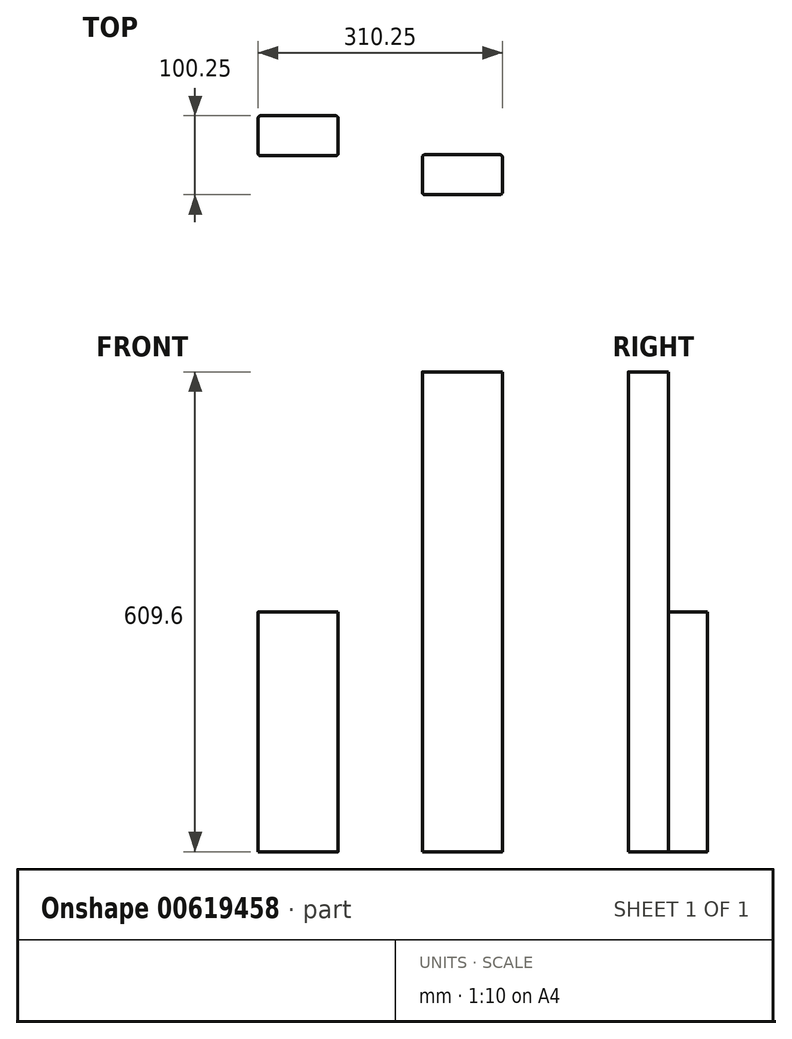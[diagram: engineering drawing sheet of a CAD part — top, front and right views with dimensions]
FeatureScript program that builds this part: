
annotation { "Feature Type Name" : "Feature", "Feature Type Description" : "" }
export const myFeature = defineFeature(function(context is Context, id is Id, definition is map)
    precondition{}
    {
        {
            var Q0;
            Q0=qCreatedBy(makeId("Top.planeOp"),FACE);
            var sketch = newSketch(context, id + "F0", { "sketchPlane" : qUnion([Q0])});
            skLineSegment(sketch, "E0.bottom", {"start": v(47.63, -25.4) * mm, "end": v(-47.63, -25.4) * mm});
            skLineSegment(sketch, "E0.top", {"start": v(47.63, 25.4) * mm, "end": v(-47.63, 25.4) * mm});
            skLineSegment(sketch, "E0.left", {"start": v(50.8, -22.22) * mm, "end": v(50.8, 22.23) * mm});
            skLineSegment(sketch, "E0.right", {"start": v(-50.8, -22.23) * mm, "end": v(-50.8, 22.22) * mm});
            skPoint(sketch, "E0.middle", {"position": v(0, 0) * mm});
            skPoint(sketch, "E1.visualSharp", {"position": v(-50.8, 25.4) * mm});
            skArc(sketch, "E1.filletArc", {"start": v(-47.63, 25.4) * mm, "mid": v(-49.87, 24.47) * mm, "end": v(-50.8, 22.22) * mm});
            skPoint(sketch, "E2.visualSharp", {"position": v(50.8, 25.4) * mm});
            skArc(sketch, "E2.filletArc", {"start": v(50.8, 22.23) * mm, "mid": v(49.87, 24.47) * mm, "end": v(47.63, 25.4) * mm});
            skPoint(sketch, "E3.visualSharp", {"position": v(50.8, -25.4) * mm});
            skArc(sketch, "E3.filletArc", {"start": v(47.63, -25.4) * mm, "mid": v(49.87, -24.47) * mm, "end": v(50.8, -22.22) * mm});
            skPoint(sketch, "E4.visualSharp", {"position": v(-50.8, -25.4) * mm});
            skArc(sketch, "E4.filletArc", {"start": v(-50.8, -22.23) * mm, "mid": v(-49.87, -24.47) * mm, "end": v(-47.63, -25.4) * mm});
            skSolve(sketch);
        }
        {
            var Q0;
            Q0 = qSketchRegion(id + "F0", true);
            extrude(context, id + "F1", {"entities" : qUnion([Q0]), "depth" : 304.8 * mm, "offsetDistance" : 25.4 * mm});
        }
        {
            var Q0;
            Q0=qCreatedBy(makeId("Top.planeOp"),FACE);
            var sketch = newSketch(context, id + "F2", { "sketchPlane" : qUnion([Q0])});
            skLineSegment(sketch, "E5.bottom", {"start": v(256.28, -74.85) * mm, "end": v(161.03, -74.85) * mm});
            skLineSegment(sketch, "E5.top", {"start": v(256.28, -24.05) * mm, "end": v(161.03, -24.05) * mm});
            skLineSegment(sketch, "E5.left", {"start": v(259.45, -71.67) * mm, "end": v(259.45, -27.22) * mm});
            skLineSegment(sketch, "E5.right", {"start": v(157.85, -71.67) * mm, "end": v(157.85, -27.22) * mm});
            skPoint(sketch, "E5.middle", {"position": v(208.65, -49.45) * mm});
            skPoint(sketch, "E6.visualSharp", {"position": v(157.85, -24.05) * mm});
            skArc(sketch, "E6.filletArc", {"start": v(161.03, -24.05) * mm, "mid": v(158.78, -24.98) * mm, "end": v(157.85, -27.22) * mm});
            skPoint(sketch, "E7.visualSharp", {"position": v(259.45, -24.05) * mm});
            skArc(sketch, "E7.filletArc", {"start": v(259.45, -27.22) * mm, "mid": v(258.52, -24.98) * mm, "end": v(256.28, -24.05) * mm});
            skPoint(sketch, "E8.visualSharp", {"position": v(259.45, -74.85) * mm});
            skArc(sketch, "E8.filletArc", {"start": v(256.28, -74.85) * mm, "mid": v(258.52, -73.92) * mm, "end": v(259.45, -71.67) * mm});
            skPoint(sketch, "E9.visualSharp", {"position": v(157.85, -74.85) * mm});
            skArc(sketch, "E9.filletArc", {"start": v(157.85, -71.67) * mm, "mid": v(158.78, -73.92) * mm, "end": v(161.03, -74.85) * mm});
            skSolve(sketch);
        }
        {
            var Q0;
            Q0 = qSketchRegion(id + "F2", true);
            extrude(context, id + "F3", {"entities" : qUnion([Q0]), "depth" : 609.6 * mm, "offsetDistance" : 25.4 * mm});
        }
    });
